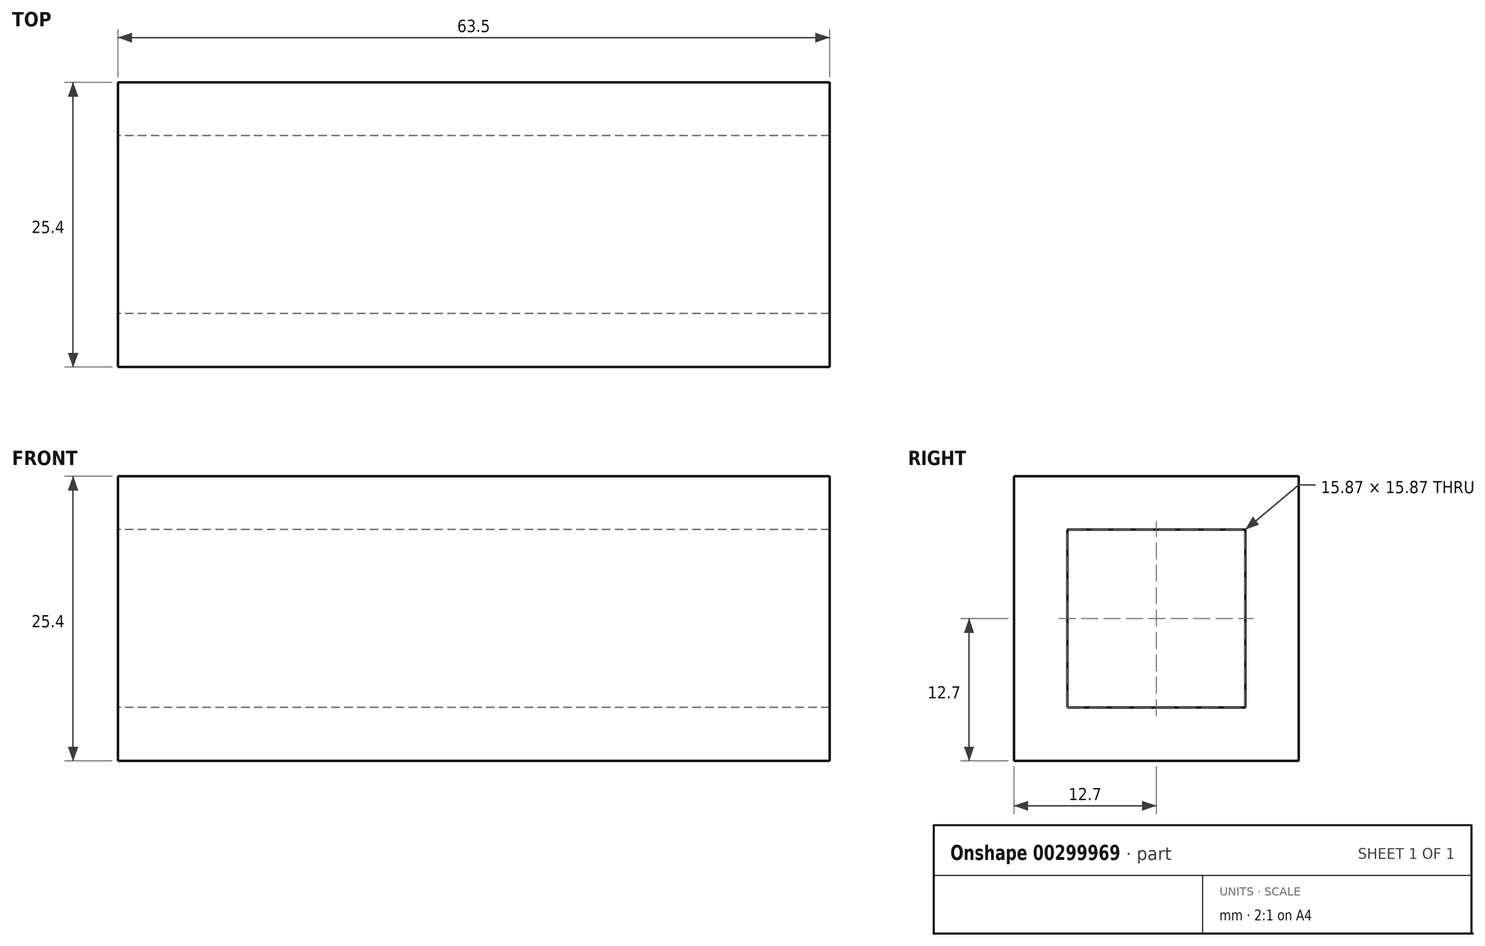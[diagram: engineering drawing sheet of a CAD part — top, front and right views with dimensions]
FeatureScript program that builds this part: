
annotation { "Feature Type Name" : "Feature", "Feature Type Description" : "" }
export const myFeature = defineFeature(function(context is Context, id is Id, definition is map)
    precondition{}
    {
        {
            var Q0;
            Q0=qCreatedBy(makeId("Right.planeOp"),FACE);
            var sketch = newSketch(context, id + "F0", { "sketchPlane" : qUnion([Q0])});
            skLineSegment(sketch, "E0.bottom", {"start": v(0, 0) * mm, "end": v(25.4, 0) * mm});
            skLineSegment(sketch, "E0.top", {"start": v(0, 25.4) * mm, "end": v(25.4, 25.4) * mm});
            skLineSegment(sketch, "E0.left", {"start": v(0, 0) * mm, "end": v(0, 25.4) * mm});
            skLineSegment(sketch, "E0.right", {"start": v(25.4, 0) * mm, "end": v(25.4, 25.4) * mm});
            skLineSegment(sketch, "E1.bottom", {"start": v(4.76, 20.64) * mm, "end": v(20.64, 20.64) * mm});
            skLineSegment(sketch, "E1.top", {"start": v(4.76, 4.76) * mm, "end": v(20.64, 4.76) * mm});
            skLineSegment(sketch, "E1.left", {"start": v(4.76, 20.64) * mm, "end": v(4.76, 4.76) * mm});
            skLineSegment(sketch, "E1.right", {"start": v(20.64, 20.64) * mm, "end": v(20.64, 4.76) * mm});
            skSolve(sketch);
        }
        {
            var Q0;
            Q0 = qSketchRegion(id + "F0", true);
            extrude(context, id + "F1", {"entities" : qUnion([Q0]), "depth" : 63.5 * mm, "offsetDistance" : 25 * mm});
        }
    });
